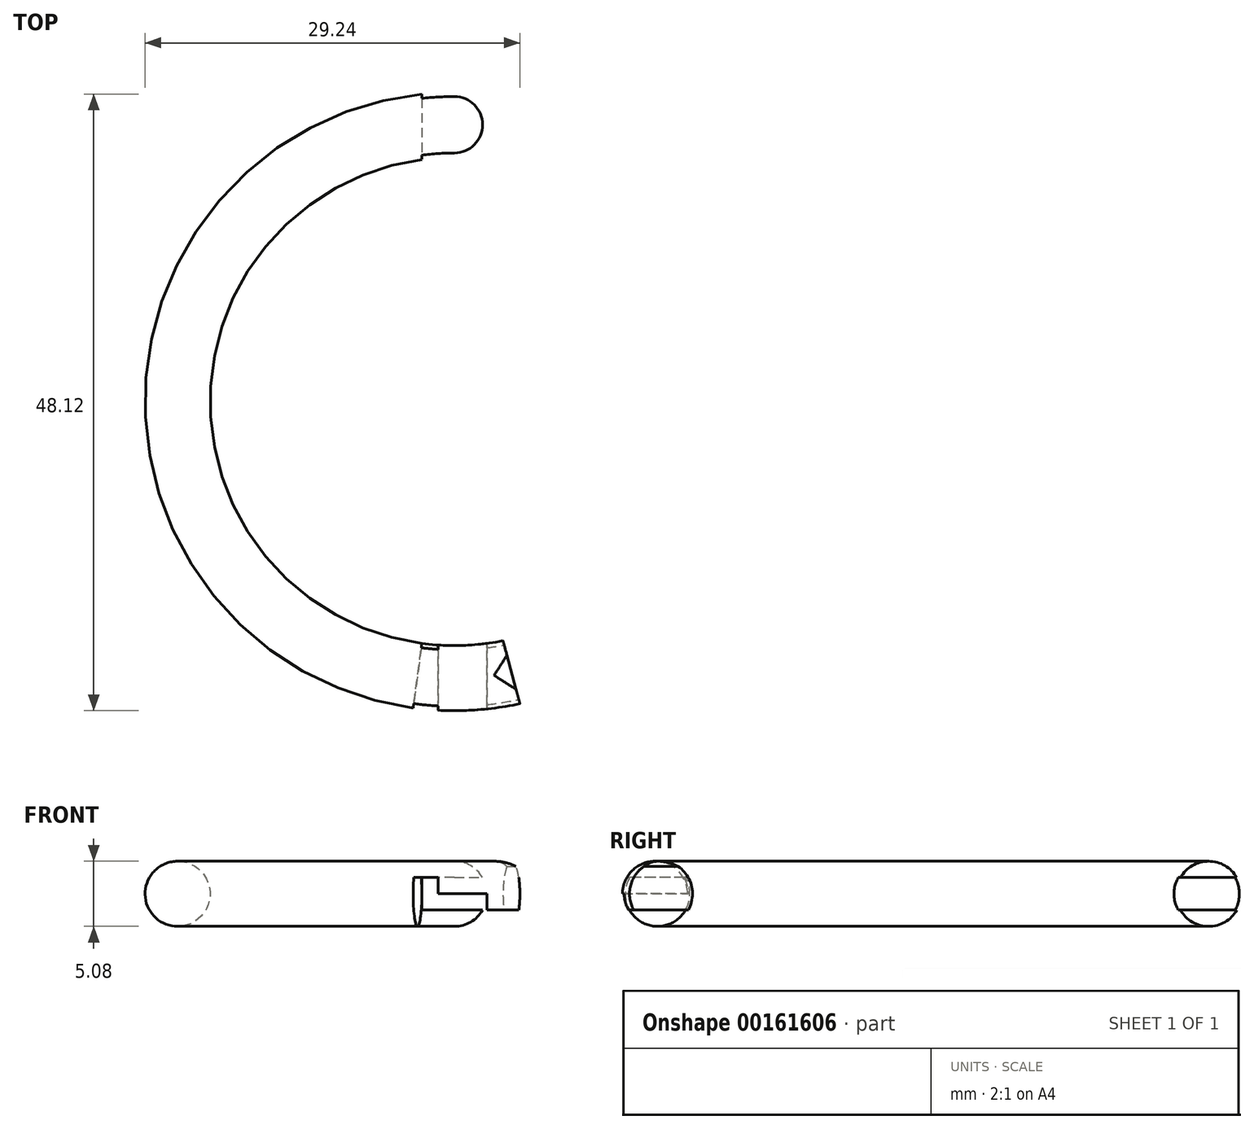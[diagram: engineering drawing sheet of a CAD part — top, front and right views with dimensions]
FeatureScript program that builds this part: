
annotation { "Feature Type Name" : "Feature", "Feature Type Description" : "" }
export const myFeature = defineFeature(function(context is Context, id is Id, definition is map)
    precondition{}
    {
        {
            var Q0;
            Q0=qCreatedBy(makeId("Top.planeOp"),FACE);
            var sketch = newSketch(context, id + "F0", { "sketchPlane" : qUnion([Q0])});
            skArc(sketch, "E0", {"start": v(0, 19.05) * mm, "mid": v(-18.89, -2.49) * mm, "end": v(4.93, -18.4) * mm});
            skArc(sketch, "E1", {"start": v(0, 24.13) * mm, "mid": v(-23.92, -3.15) * mm, "end": v(6.25, -23.3) * mm});
            skArc(sketch, "E2", {"start": v(0, 19.05) * mm, "mid": v(2.54, 21.6) * mm, "end": v(0, 24.13) * mm});
            skLineSegment(sketch, "E3", {"start": v(0, 0) * mm, "end": v(6.25, -23.3) * mm});
            skLineSegment(sketch, "E4", {"start": v(0, 0) * mm, "end": v(0, -24.13) * mm, "construction": true});
            skSolve(sketch);
        }
        {
            var Q0;
            Q0 = qSketchRegion(id + "F0", true);
            extrude(context, id + "F1", {"entities" : qUnion([Q0]), "depth" : 5.08 * mm});
        }
        {
            var Q0;
            Q0=makeQuery(id+"F1.opExtrude","CAP_FACE",FACE,{"disambiguationData":[OSD([sQuery(id+"F0.wireOp",EDGE,"E0"),sQuery(id+"F0.wireOp",EDGE,"E1"),sQuery(id+"F0.wireOp",EDGE,"E2"),sQuery(id+"F0.wireOp",EDGE,"7r3T7DYV-JdIa-RgLA-PCdA-LdlWGYxwMqZf")])],"isStart":false});
            var Q1;
            Q1=makeQuery(id+"F1.opExtrude","CAP_FACE",FACE,{"disambiguationData":[OSD([sQuery(id+"F0.wireOp",EDGE,"E0"),sQuery(id+"F0.wireOp",EDGE,"E1"),sQuery(id+"F0.wireOp",EDGE,"E2"),sQuery(id+"F0.wireOp",EDGE,"7r3T7DYV-JdIa-RgLA-PCdA-LdlWGYxwMqZf")])],"isStart":true});
            fillet(context, id + "F2", {"entities" : qUnion([Q0, Q1]), "radius" : 2.54 * mm, "tangentPropagation" : true, "allowEdgeOverflow" : false});
        }
        {
            var Q0;
            Q0=qCreatedBy(makeId("Top.planeOp"),FACE);
            cPlane(context, id + "F3", {"entities" : qUnion([Q0]), "cplaneType" : CPlaneType.OFFSET, "offset" : 2.54 * mm, "width" : 152.4 * mm, "height" : 152.4 * mm});
        }
        {
            var Q0;
            Q0=qCreatedBy(id+"F3.planeOp",FACE);
            var sketch = newSketch(context, id + "F4", { "sketchPlane" : qUnion([Q0])});
            skLineSegment(sketch, "E5.bottom", {"start": v(2.54, -17.78) * mm, "end": v(-2.54, -17.78) * mm});
            skLineSegment(sketch, "E5.top", {"start": v(2.54, -25.4) * mm, "end": v(-2.54, -25.4) * mm});
            skLineSegment(sketch, "E5.left", {"start": v(2.54, -17.78) * mm, "end": v(2.54, -25.4) * mm});
            skLineSegment(sketch, "E5.right", {"start": v(-2.54, -17.78) * mm, "end": v(-2.54, -25.4) * mm});
            skPoint(sketch, "E5.middle", {"position": v(0, -21.59) * mm});
            skSolve(sketch);
        }
        {
            var Q0;
            Q0 = qSketchRegion(id + "F4", true);
            extrude(context, id + "F5", {"entities" : qUnion([Q0]), "operationType" : NewBodyOperationType.REMOVE, "oppositeDirection" : true, "depth" : 25.4 * mm});
        }
        {
            var Q0;
            Q0=qCreatedBy(id+"F3.planeOp",FACE);
            var sketch = newSketch(context, id + "F6", { "sketchPlane" : qUnion([Q0])});
            skLineSegment(sketch, "E6.bottom", {"start": v(-2.54, 25.4) * mm, "end": v(2.54, 25.4) * mm});
            skLineSegment(sketch, "E6.top", {"start": v(-2.54, 17.78) * mm, "end": v(2.54, 17.78) * mm});
            skLineSegment(sketch, "E6.left", {"start": v(-2.54, 25.4) * mm, "end": v(-2.54, 17.78) * mm});
            skLineSegment(sketch, "E6.right", {"start": v(2.54, 25.4) * mm, "end": v(2.54, 17.78) * mm});
            skPoint(sketch, "E6.middle", {"position": v(0, 21.6) * mm});
            skSolve(sketch);
        }
        {
            var Q0;
            Q0 = qSketchRegion(id + "F6", true);
            extrude(context, id + "F7", {"entities" : qUnion([Q0]), "operationType" : NewBodyOperationType.REMOVE, "depth" : 1.27 * mm, "hasSecondDirection" : true, "secondDirectionOppositeDirection" : true, "secondDirectionDepth" : 1.27 * mm});
        }
        {
            var Q0;
            Q0=makeQuery(id+"F5.boolean.opBoolean","COPY",FACE,{"derivedFrom":makeQuery(id+"F5.opExtrude","CAP_FACE",FACE,{"disambiguationData":[OSD([sQuery(id+"F4.wireOp",EDGE,"E5.bottom"),sQuery(id+"F4.wireOp",EDGE,"E5.top"),sQuery(id+"F4.wireOp",EDGE,"E5.left"),sQuery(id+"F4.wireOp",EDGE,"E5.right")])],"isStart":true})});
            var sketch = newSketch(context, id + "F8", { "sketchPlane" : qUnion([Q0])});
            skLineSegment(sketch, "E7", {"start": v(-1.27, 19) * mm, "end": v(-1.27, 24.1) * mm});
            skPoint(sketch, "E8.orphan", {"position": v(2.54, 18.88) * mm});
            skPoint(sketch, "E9.orphan", {"position": v(2.54, 24) * mm});
            skPoint(sketch, "E10.orphan", {"position": v(-2.54, 18.88) * mm});
            skLineSegment(sketch, "E11", {"start": v(-2.54, 18.88) * mm, "end": v(-3.22, 23.91) * mm});
            skLineSegment(sketch, "E12", {"start": v(-3.5, 23.88) * mm, "end": v(-2.94, 23.95) * mm, "construction": true});
            skArc(sketch, "E13", {"start": v(-1.27, 19) * mm, "mid": v(-1.9, 18.95) * mm, "end": v(-2.54, 18.88) * mm});
            skArc(sketch, "E14", {"start": v(-1.27, 24.1) * mm, "mid": v(-2.25, 24.03) * mm, "end": v(-3.22, 23.91) * mm});
            skSolve(sketch);
        }
        {
            var Q0;
            Q0 = qSketchRegion(id + "F8", true);
            extrude(context, id + "F9", {"entities" : qUnion([Q0]), "operationType" : NewBodyOperationType.REMOVE, "oppositeDirection" : true, "depth" : 1.27 * mm, "hasSecondDirection" : true, "secondDirectionOppositeDirection" : false, "secondDirectionDepth" : 25.4 * mm});
        }
        {
            var Q0;
            Q0=qCreatedBy(makeId("Top.planeOp"),FACE);
            cPlane(context, id + "F10", {"entities" : qUnion([Q0]), "cplaneType" : CPlaneType.OFFSET, "offset" : 1.27 * mm, "width" : 152.4 * mm, "height" : 152.4 * mm});
        }
        {
            var Q0;
            Q0=qCreatedBy(id+"F10.planeOp",FACE);
            var sketch = newSketch(context, id + "F11", { "sketchPlane" : qUnion([Q0])});
            skLineSegment(sketch, "E15.bottom", {"start": v(2.54, -24) * mm, "end": v(6.25, -24) * mm});
            skLineSegment(sketch, "E15.top", {"start": v(2.54, -18.4) * mm, "end": v(6.25, -18.4) * mm});
            skLineSegment(sketch, "E15.left", {"start": v(2.54, -24) * mm, "end": v(2.54, -18.4) * mm});
            skLineSegment(sketch, "E15.right", {"start": v(6.25, -24) * mm, "end": v(6.25, -18.4) * mm});
            skSolve(sketch);
        }
        {
            var Q0;
            Q0 = qSketchRegion(id + "F11", true);
            extrude(context, id + "F12", {"entities" : qUnion([Q0]), "operationType" : NewBodyOperationType.REMOVE, "oppositeDirection" : true, "depth" : 1.27 * mm});
        }
        {
            var Q0;
            Q0=qCreatedBy(id+"F10.planeOp",FACE);
            var sketch = newSketch(context, id + "F13", { "sketchPlane" : qUnion([Q0])});
            skArc(sketch, "E16", {"start": v(2.54, -24) * mm, "mid": v(4.4, -23.72) * mm, "end": v(6.25, -23.3) * mm});
            skArc(sketch, "E17", {"start": v(2.54, -18.88) * mm, "mid": v(3.74, -18.68) * mm, "end": v(4.93, -18.4) * mm});
            skLineSegment(sketch, "E18", {"start": v(2.54, -24) * mm, "end": v(2.54, -18.88) * mm, "construction": true});
            skLineSegment(sketch, "E19", {"start": v(4.93, -18.4) * mm, "end": v(6.25, -23.3) * mm});
            skLineSegment(sketch, "E20", {"start": v(3.8, -18.67) * mm, "end": v(5.1, -23.58) * mm});
            skSolve(sketch);
        }
        {
            var Q0;
            {var subQ0=sQuery(id+"F13.wireOp",EDGE,"E19");Q0=makeQuery(id+"F13.imprint","IMPRINT",FACE,{"disambiguationData":[TD([[makeQuery(id+"F13.imprint","IMPRINT",EDGE,{"derivedFrom":subQ0}),-1.0]])]});}
            extrude(context, id + "F14", {"entities" : qUnion([Q0]), "operationType" : NewBodyOperationType.REMOVE, "depth" : 25.4 * mm});
        }
    });
